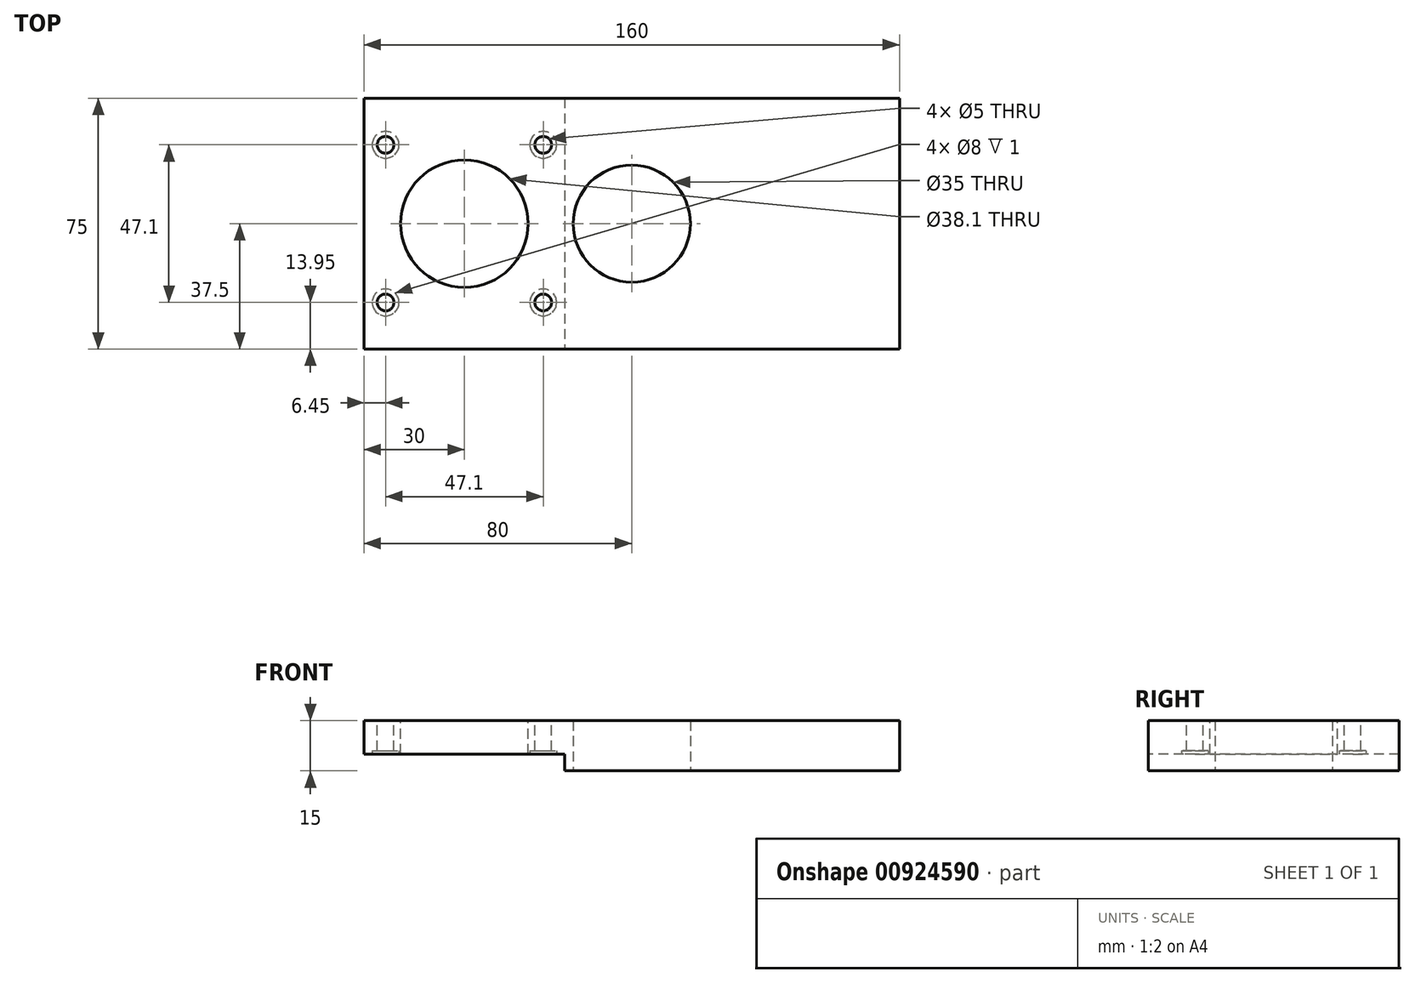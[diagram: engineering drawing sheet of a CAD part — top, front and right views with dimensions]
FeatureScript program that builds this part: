
annotation { "Feature Type Name" : "Feature", "Feature Type Description" : "" }
export const myFeature = defineFeature(function(context is Context, id is Id, definition is map)
    precondition{}
    {
        {
            var Q0;
            Q0=qCreatedBy(makeId("Top.planeOp"),FACE);
            var sketch = newSketch(context, id + "F0", { "sketchPlane" : qUnion([Q0])});
            skCircle(sketch, "E0", {"center": v(0, 0) * mm, "radius": 17.5 * mm});
            skLineSegment(sketch, "E1.bottom", {"start": v(80, -37.5) * mm, "end": v(-80, -37.5) * mm});
            skLineSegment(sketch, "E1.top", {"start": v(80, 37.5) * mm, "end": v(-80, 37.5) * mm});
            skLineSegment(sketch, "E1.left", {"start": v(80, -37.5) * mm, "end": v(80, 37.5) * mm});
            skLineSegment(sketch, "E1.right", {"start": v(-80, -37.5) * mm, "end": v(-80, 37.5) * mm});
            skSolve(sketch);
        }
        {
            var Q0;
            Q0=makeQuery(id+"F0.imprint","IMPRINT",FACE,{"disambiguationData":[TD([[makeQuery(id+"F0.imprint","IMPRINT",EDGE,{"derivedFrom":sQuery(id+"F0.wireOp",EDGE,"HPr2vzE0-l0NK-PHcw-MCR2-NGBl1DphhECB")}),1.0]])]});
            var Q1;
            Q1=makeQuery(id+"F0.imprint","IMPRINT",FACE,{"disambiguationData":[TD([[makeQuery(id+"F0.imprint","IMPRINT",EDGE,{"derivedFrom":sQuery(id+"F0.wireOp",EDGE,"E0")}),-1.0]])]});
            extrude(context, id + "F1", {"entities" : qUnion([Q0, Q1]), "depth" : 15 * mm, "offsetDistance" : 25 * mm});
        }
        {
            var Q0;
            Q0=makeQuery(id+"F1.opExtrude","CAP_FACE",FACE,{"disambiguationData":[OSD([sQuery(id+"F0.wireOp",EDGE,"E0"),sQuery(id+"F0.wireOp",EDGE,"E1.bottom"),sQuery(id+"F0.wireOp",EDGE,"E1.top"),sQuery(id+"F0.wireOp",EDGE,"E1.left"),sQuery(id+"F0.wireOp",EDGE,"E1.right")])],"isStart":false});
            var sketch = newSketch(context, id + "F2", { "sketchPlane" : qUnion([Q0])});
            skLineSegment(sketch, "E2.bottom", {"start": v(-26.45, -23.55) * mm, "end": v(-73.55, -23.55) * mm, "construction": true});
            skLineSegment(sketch, "E2.top", {"start": v(-26.45, 23.55) * mm, "end": v(-73.55, 23.55) * mm, "construction": true});
            skLineSegment(sketch, "E2.left", {"start": v(-26.45, -23.55) * mm, "end": v(-26.45, 23.55) * mm, "construction": true});
            skLineSegment(sketch, "E2.right", {"start": v(-73.55, -23.55) * mm, "end": v(-73.55, 23.55) * mm, "construction": true});
            skPoint(sketch, "E2.middle", {"position": v(-50, 0) * mm});
            skCircle(sketch, "E3", {"center": v(-73.55, 23.55) * mm, "radius": 2.5 * mm});
            skCircle(sketch, "E4", {"center": v(-26.45, 23.55) * mm, "radius": 2.5 * mm});
            skCircle(sketch, "E5", {"center": v(-26.45, -23.55) * mm, "radius": 2.5 * mm});
            skCircle(sketch, "E6", {"center": v(-73.55, -23.55) * mm, "radius": 2.5 * mm});
            skCircle(sketch, "E7", {"center": v(-50, 0) * mm, "radius": 19.05 * mm});
            skSolve(sketch);
        }
        {
            var Q0;
            Q0 = qSketchRegion(id + "F2", true);
            extrude(context, id + "F3", {"entities" : qUnion([Q0]), "operationType" : NewBodyOperationType.REMOVE, "oppositeDirection" : true, "depth" : 25 * mm, "offsetDistance" : 25 * mm});
        }
        {
            var Q0;
            Q0=makeQuery(id+"F1.opExtrude","CAP_FACE",FACE,{"disambiguationData":[OSD([sQuery(id+"F0.wireOp",EDGE,"E0"),sQuery(id+"F0.wireOp",EDGE,"E1.bottom"),sQuery(id+"F0.wireOp",EDGE,"E1.top"),sQuery(id+"F0.wireOp",EDGE,"E1.left"),sQuery(id+"F0.wireOp",EDGE,"E1.right")])],"isStart":true});
            var sketch = newSketch(context, id + "F4", { "sketchPlane" : qUnion([Q0])});
            skCircle(sketch, "E8", {"center": v(-73.55, 23.55) * mm, "radius": 4 * mm});
            skCircle(sketch, "E9", {"center": v(-26.45, 23.55) * mm, "radius": 4 * mm});
            skCircle(sketch, "E10", {"center": v(-26.45, -23.55) * mm, "radius": 4 * mm});
            skCircle(sketch, "E11", {"center": v(-73.55, -23.55) * mm, "radius": 4 * mm});
            skSolve(sketch);
        }
        {
            var Q0;
            Q0 = qSketchRegion(id + "F4", true);
            extrude(context, id + "F5", {"entities" : qUnion([Q0]), "operationType" : NewBodyOperationType.REMOVE, "oppositeDirection" : true, "depth" : 6 * mm, "offsetDistance" : 25 * mm});
        }
        {
            var Q0;
            Q0=makeQuery(id+"F1.opExtrude","SWEPT_FACE",FACE,{"disambiguationData":[OSD([sQuery(id+"F0.wireOp",EDGE,"E1.bottom")])]});
            var sketch = newSketch(context, id + "F6", { "sketchPlane" : qUnion([Q0])});
            skLineSegment(sketch, "E12.bottom", {"start": v(-20, 0) * mm, "end": v(-80, 0) * mm});
            skLineSegment(sketch, "E12.top", {"start": v(-20, 5) * mm, "end": v(-80, 5) * mm});
            skLineSegment(sketch, "E12.left", {"start": v(-20, 0) * mm, "end": v(-20, 5) * mm});
            skLineSegment(sketch, "E12.right", {"start": v(-80, 0) * mm, "end": v(-80, 5) * mm});
            skSolve(sketch);
        }
        {
            var Q0;
            Q0=makeQuery(id+"F6.imprint","IMPRINT",FACE,{"disambiguationData":[TD([[makeQuery(id+"F6.imprint","IMPRINT",EDGE,{"derivedFrom":sQuery(id+"F6.wireOp",EDGE,"E12.bottom")}),-1.0]])]});
            extrude(context, id + "F7", {"entities" : qUnion([Q0]), "operationType" : NewBodyOperationType.REMOVE, "oppositeDirection" : true, "depth" : 79.7 * mm, "offsetDistance" : 25 * mm});
        }
    });
